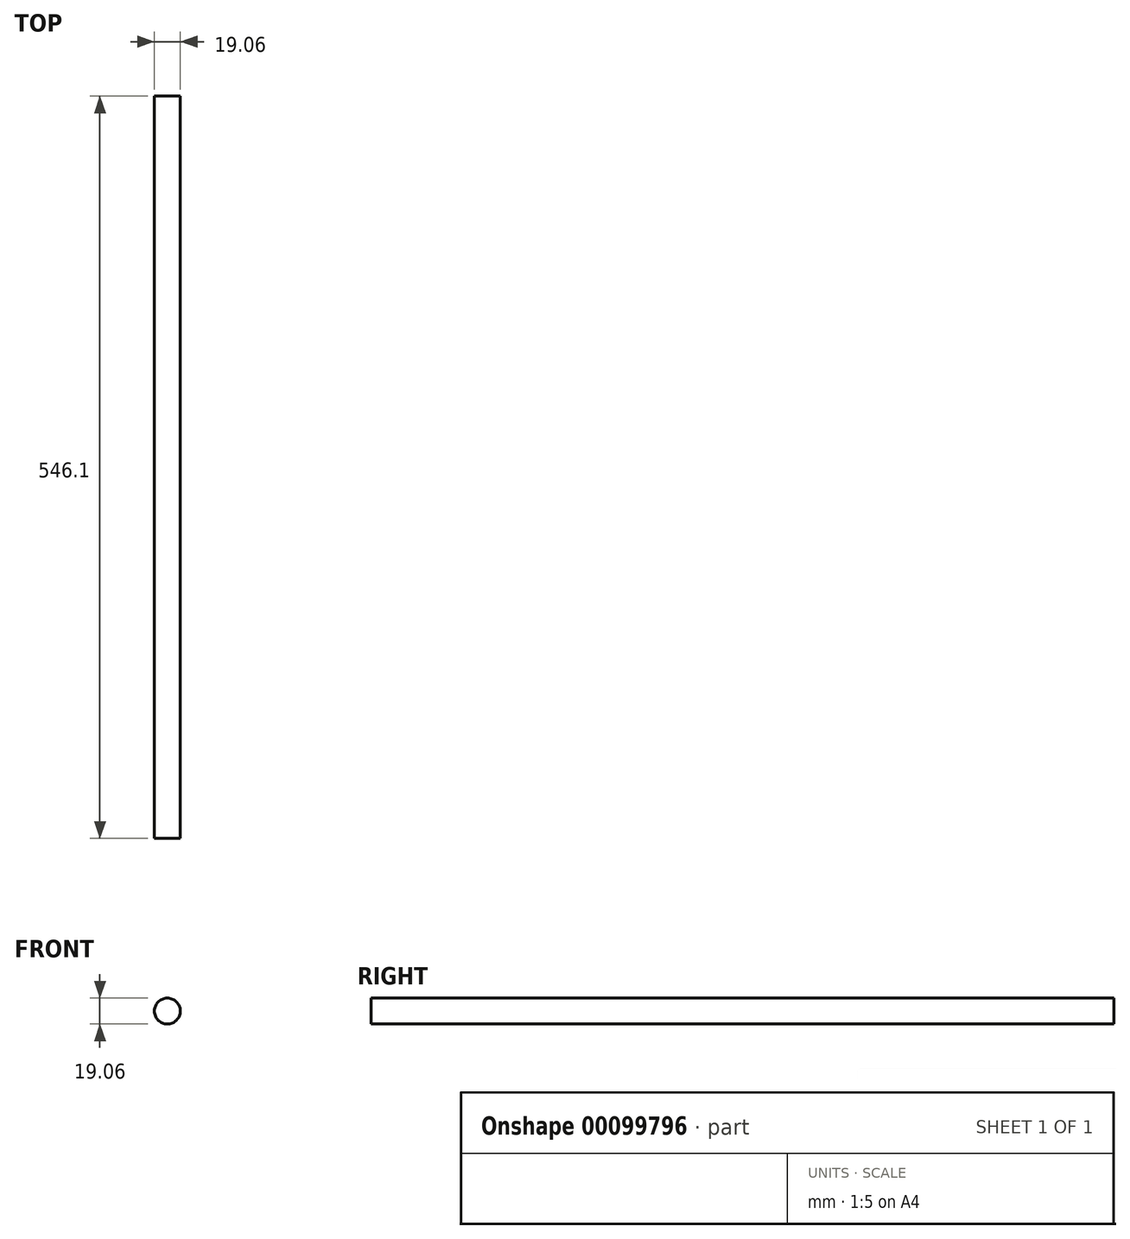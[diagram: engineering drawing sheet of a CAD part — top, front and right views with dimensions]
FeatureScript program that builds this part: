
annotation { "Feature Type Name" : "Feature", "Feature Type Description" : "" }
export const myFeature = defineFeature(function(context is Context, id is Id, definition is map)
    precondition{}
    {
        {
            var Q0;
            Q0=qCreatedBy(makeId("Front.planeOp"),FACE);
            var sketch = newSketch(context, id + "F0", { "sketchPlane" : qUnion([Q0])});
            skCircle(sketch, "E0", {"center": v(0, 0) * mm, "radius": 9.53 * mm});
            skSolve(sketch);
        }
        {
            var Q0;
            Q0=makeQuery(id+"F0.imprint","IMPRINT",FACE,{"disambiguationData":[TD([[makeQuery(id+"F0.imprint","IMPRINT",EDGE,{"derivedFrom":sQuery(id+"F0.wireOp",EDGE,"E0")}),1.0]])]});
            extrude(context, id + "F1", {"entities" : qUnion([Q0]), "depth" : 546.1 * mm});
        }
    });
